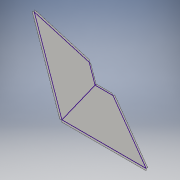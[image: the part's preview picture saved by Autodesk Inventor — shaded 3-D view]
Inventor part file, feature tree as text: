
AUTODESK INVENTOR PART (.ipt)
format: ipt  version: 2016 (Build 200138000, 138)  size: 165,376 bytes
history: native  units: in
note: dims shown in document units (in); Inventor stores cm internally (conversion verified against a paired STEP export)
features: sketch x3, extrude x2
ambient origin geometry x8: Origin, YZ Plane, XZ Plane, XY Plane, X Axis, Y Axis, Z Axis, Center Point
bodies: Body1 (feature_tree)
feature tree (5):
  extrude  "Extrusion2"  Depth=11.75in
  extrude  "Extrusion4"  Depth=7.9775in
  sketch  "Sketch5"  dims[d5=7.9775in d31=0.8619in d32=0.8619in d33=0.3749in d34=0.3749in d35=0.375in d36=11.75in d37=0.8619in d38=2.5in d39=7.9779in d40=0.3749in d41=0.8619in d42=0.005in d43=0.0in d45=0.375in d46=0.2in d47=0.375in d48=0.375in d51=0.2in d66=0.3in d67=90.0deg d68=0.3in d72=90.0deg d73=0.3in d76=0.3in d77=90.0deg d80=90.0deg d81=0.3in d82=90.0deg d83=0.3in d84=0.3in d85=0.3in d86=0.005in d87=0.0in]
  sketch  "Sketch1"  dims[d1=11.75in d2=2.5in]
  sketch  "Sketch3"  dims[d3=6.5in d4=7.9775in]
